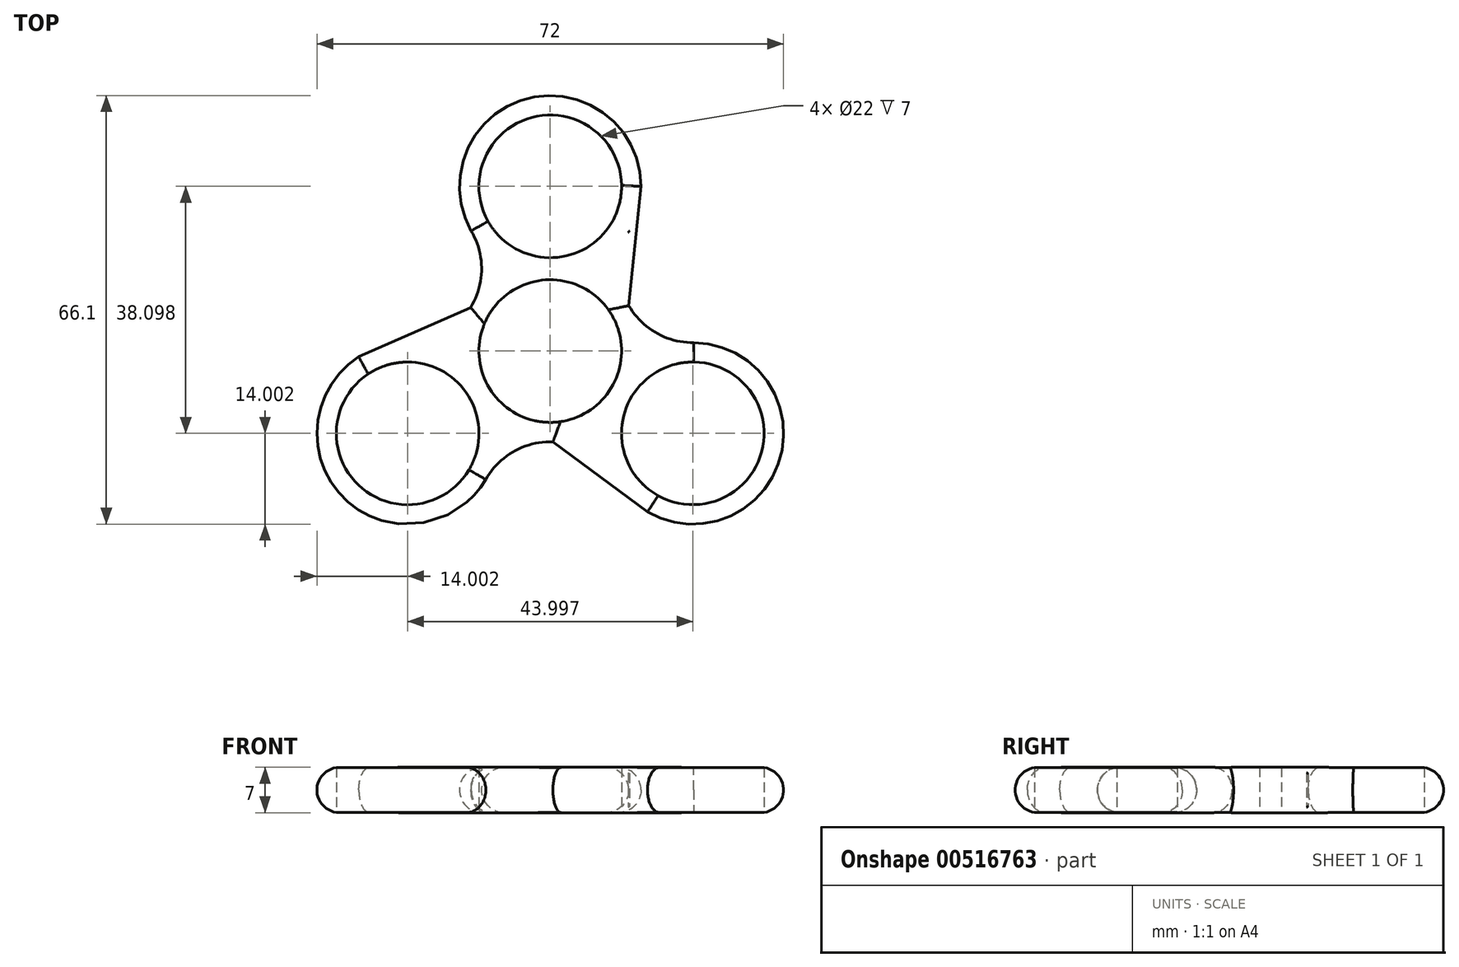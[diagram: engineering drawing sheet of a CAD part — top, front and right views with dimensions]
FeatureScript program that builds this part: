
annotation { "Feature Type Name" : "Feature", "Feature Type Description" : "" }
export const myFeature = defineFeature(function(context is Context, id is Id, definition is map)
    precondition{}
    {
        {
            var Q0;
            Q0=qCreatedBy(makeId("Top.planeOp"),FACE);
            var sketch = newSketch(context, id + "F0", { "sketchPlane" : qUnion([Q0])});
            skCircle(sketch, "E0", {"center": v(0, 0) * mm, "radius": 11 * mm});
            skCircle(sketch, "E1", {"center": v(0, 25.4) * mm, "radius": 11 * mm});
            skArc(sketch, "E2", {"start": v(12.05, 18.28) * mm, "mid": v(12.12, 18.4) * mm, "end": v(12.2, 18.52) * mm});
            skArc(sketch, "E3", {"start": v(12.42, -22.91) * mm, "mid": v(35.04, -17.78) * mm, "end": v(21.86, 1.3) * mm});
            skCircle(sketch, "E4", {"center": v(22, -12.7) * mm, "radius": 11 * mm});
            skCircle(sketch, "E5", {"center": v(-22, -12.7) * mm, "radius": 11 * mm});
            skArc(sketch, "E6", {"start": v(-21.25, 1.28) * mm, "mid": v(-22, 1.3) * mm, "end": v(-22.76, 1.28) * mm});
            skArc(sketch, "E7", {"start": v(12.2, 18.52) * mm, "mid": v(12.12, 18.4) * mm, "end": v(12.05, 18.28) * mm});
            skArc(sketch, "E8", {"start": v(9.94, -19.82) * mm, "mid": v(9.88, -19.7) * mm, "end": v(9.8, -19.58) * mm});
            skPoint(sketch, "E9.orphan", {"position": v(8.05, -11.45) * mm});
            skPoint(sketch, "E10.orphan", {"position": v(-8.05, -11.45) * mm});
            skPoint(sketch, "E11.orphan", {"position": v(13.94, -1.25) * mm});
            skPoint(sketch, "E12.orphan", {"position": v(5.9, 12.7) * mm});
            skPoint(sketch, "E13.orphan", {"position": v(-5.9, 12.7) * mm});
            skPoint(sketch, "E14.orphan", {"position": v(-14.46, -0.9) * mm});
            skPoint(sketch, "E15.endSnap0", {"position": v(-12.27, 6.71) * mm});
            skLineSegment(sketch, "E16", {"start": v(15, -24.82) * mm, "end": v(0.4, -14) * mm});
            skPoint(sketch, "E16.endSnap0", {"position": v(0, -14) * mm});
            skLineSegment(sketch, "E17", {"start": v(-29.53, -0.9) * mm, "end": v(-12.27, 6.71) * mm});
            skLineSegment(sketch, "E18", {"start": v(14, 25.4) * mm, "end": v(12.12, 7) * mm});
            skArc(sketch, "E19.trimOffspring", {"start": v(0.42, -14) * mm, "mid": v(-5.58, -15.46) * mm, "end": v(-9.94, -19.82) * mm});
            skArc(sketch, "E20.trimOffspring", {"start": v(13.71, 22.57) * mm, "mid": v(-2.3, 39.2) * mm, "end": v(-12.05, 18.27) * mm});
            skArc(sketch, "E21.trimOffspring", {"start": v(12.12, 7) * mm, "mid": v(16.36, 2.8) * mm, "end": v(22.14, 1.3) * mm});
            skArc(sketch, "E22.trimOffspring", {"start": v(-12.27, 6.71) * mm, "mid": v(-10.59, 12.6) * mm, "end": v(-12.2, 18.52) * mm});
            skArc(sketch, "E23.trimOffspring", {"start": v(-25.63, 0.82) * mm, "mid": v(-33.06, -21.27) * mm, "end": v(-9.8, -19.58) * mm});
            skSolve(sketch);
        }
        {
            var Q0;
            Q0=makeQuery(id+"F0.imprint","IMPRINT",FACE,{"disambiguationData":[TD([[makeQuery(id+"F0.imprint","IMPRINT",EDGE,{"derivedFrom":sQuery(id+"F0.wireOp",EDGE,"E0")}),-1.0]])]});
            extrude(context, id + "F1", {"entities" : qUnion([Q0]), "depth" : 7 * mm, "offsetDistance" : 25.4 * mm});
        }
        {
            var Q0;
            Q0=makeQuery(id+"F1.opExtrude","CAP_EDGE",EDGE,{"disambiguationData":[OSD([sQuery(id+"F0.wireOp",EDGE,"E18")])],"isStart":false});
            var Q1;
            Q1=makeQuery(id+"F1.opExtrude","CAP_EDGE",EDGE,{"disambiguationData":[OSD([sQuery(id+"F0.wireOp",EDGE,"E20.trimOffspring")])],"isStart":false});
            var Q2;
            Q2=makeQuery(id+"F1.opExtrude","CAP_EDGE",EDGE,{"disambiguationData":[OSD([sQuery(id+"F0.wireOp",EDGE,"E22.trimOffspring")])],"isStart":false});
            var Q3;
            Q3=makeQuery(id+"F1.opExtrude","CAP_EDGE",EDGE,{"disambiguationData":[OSD([sQuery(id+"F0.wireOp",EDGE,"E17")])],"isStart":false});
            var Q4;
            Q4=makeQuery(id+"F1.opExtrude","CAP_EDGE",EDGE,{"disambiguationData":[OSD([sQuery(id+"F0.wireOp",EDGE,"E23.trimOffspring")])],"isStart":false});
            var Q5;
            Q5=makeQuery(id+"F1.opExtrude","CAP_EDGE",EDGE,{"disambiguationData":[OSD([sQuery(id+"F0.wireOp",EDGE,"E19.trimOffspring")])],"isStart":false});
            var Q6;
            Q6=makeQuery(id+"F1.opExtrude","CAP_EDGE",EDGE,{"disambiguationData":[OSD([sQuery(id+"F0.wireOp",EDGE,"E16")])],"isStart":false});
            var Q7;
            Q7=makeQuery(id+"F1.opExtrude","CAP_EDGE",EDGE,{"disambiguationData":[OSD([sQuery(id+"F0.wireOp",EDGE,"E3")])],"isStart":false});
            var Q8;
            Q8=makeQuery(id+"F1.opExtrude","CAP_EDGE",EDGE,{"disambiguationData":[OSD([sQuery(id+"F0.wireOp",EDGE,"E21.trimOffspring")])],"isStart":false});
            var Q9;
            Q9=makeQuery(id+"F1.opExtrude","CAP_EDGE",EDGE,{"disambiguationData":[OSD([sQuery(id+"F0.wireOp",EDGE,"E20.trimOffspring")])],"isStart":true});
            var Q10;
            Q10=makeQuery(id+"F1.opExtrude","CAP_EDGE",EDGE,{"disambiguationData":[OSD([sQuery(id+"F0.wireOp",EDGE,"E22.trimOffspring")])],"isStart":true});
            var Q11;
            Q11=makeQuery(id+"F1.opExtrude","CAP_EDGE",EDGE,{"disambiguationData":[OSD([sQuery(id+"F0.wireOp",EDGE,"E17")])],"isStart":true});
            var Q12;
            Q12=makeQuery(id+"F1.opExtrude","CAP_EDGE",EDGE,{"disambiguationData":[OSD([sQuery(id+"F0.wireOp",EDGE,"E23.trimOffspring")])],"isStart":true});
            var Q13;
            Q13=makeQuery(id+"F1.opExtrude","CAP_EDGE",EDGE,{"disambiguationData":[OSD([sQuery(id+"F0.wireOp",EDGE,"E19.trimOffspring")])],"isStart":true});
            var Q14;
            Q14=makeQuery(id+"F1.opExtrude","CAP_EDGE",EDGE,{"disambiguationData":[OSD([sQuery(id+"F0.wireOp",EDGE,"E16")])],"isStart":true});
            var Q15;
            Q15=makeQuery(id+"F1.opExtrude","CAP_EDGE",EDGE,{"disambiguationData":[OSD([sQuery(id+"F0.wireOp",EDGE,"E3")])],"isStart":true});
            var Q16;
            Q16=makeQuery(id+"F1.opExtrude","CAP_EDGE",EDGE,{"disambiguationData":[OSD([sQuery(id+"F0.wireOp",EDGE,"E21.trimOffspring")])],"isStart":true});
            var Q17;
            Q17=makeQuery(id+"F1.opExtrude","CAP_EDGE",EDGE,{"disambiguationData":[OSD([sQuery(id+"F0.wireOp",EDGE,"E18")])],"isStart":true});
            fillet(context, id + "F2", {"entities" : qUnion([Q0, Q1, Q2, Q3, Q4, Q5, Q6, Q7, Q8, Q9, Q10, Q11, Q12, Q13, Q14, Q15, Q16, Q17]), "radius" : 3.5 * mm, "tangentPropagation" : true, "allowEdgeOverflow" : false});
        }
    });
